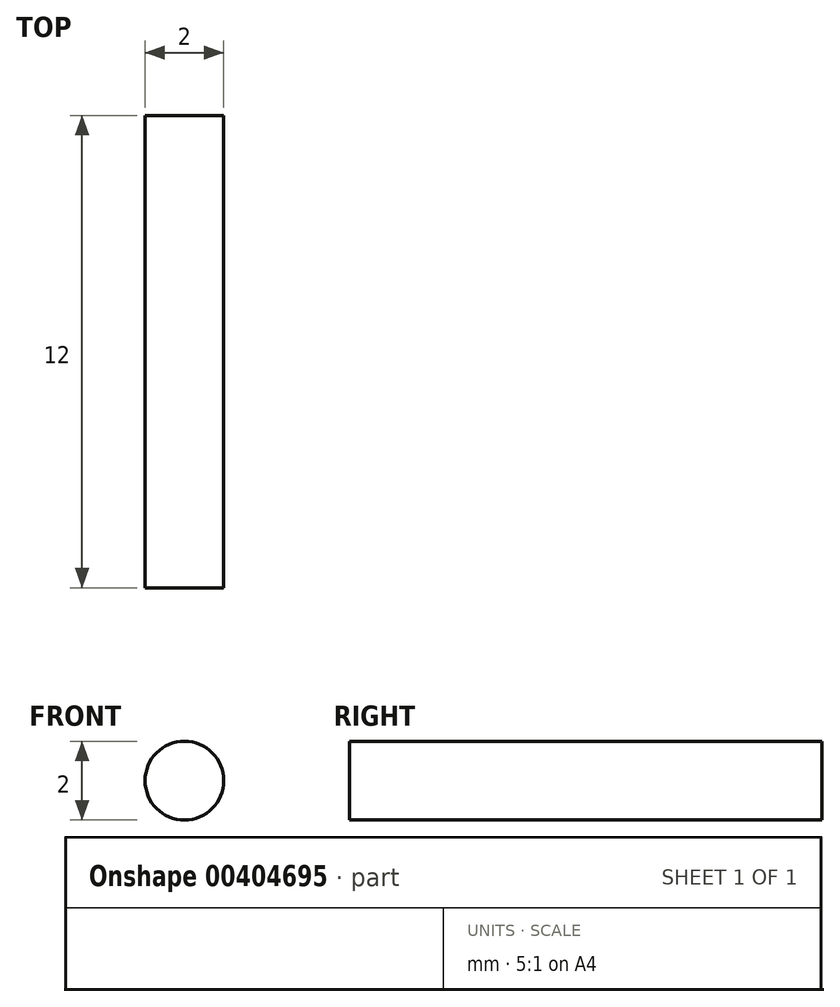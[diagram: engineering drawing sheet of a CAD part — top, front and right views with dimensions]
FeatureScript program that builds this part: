
annotation { "Feature Type Name" : "Feature", "Feature Type Description" : "" }
export const myFeature = defineFeature(function(context is Context, id is Id, definition is map)
    precondition{}
    {
        {
            var Q0;
            Q0=qCreatedBy(makeId("Front.planeOp"),FACE);
            var sketch = newSketch(context, id + "F0", { "sketchPlane" : qUnion([Q0])});
            skCircle(sketch, "E0", {"center": v(0, 0) * mm, "radius": 1 * mm});
            skSolve(sketch);
        }
        {
            var Q0;
            Q0 = qSketchRegion(id + "F0", true);
            extrude(context, id + "F1", {"entities" : qUnion([Q0]), "depth" : 12 * mm, "symmetric" : true});
        }
    });
